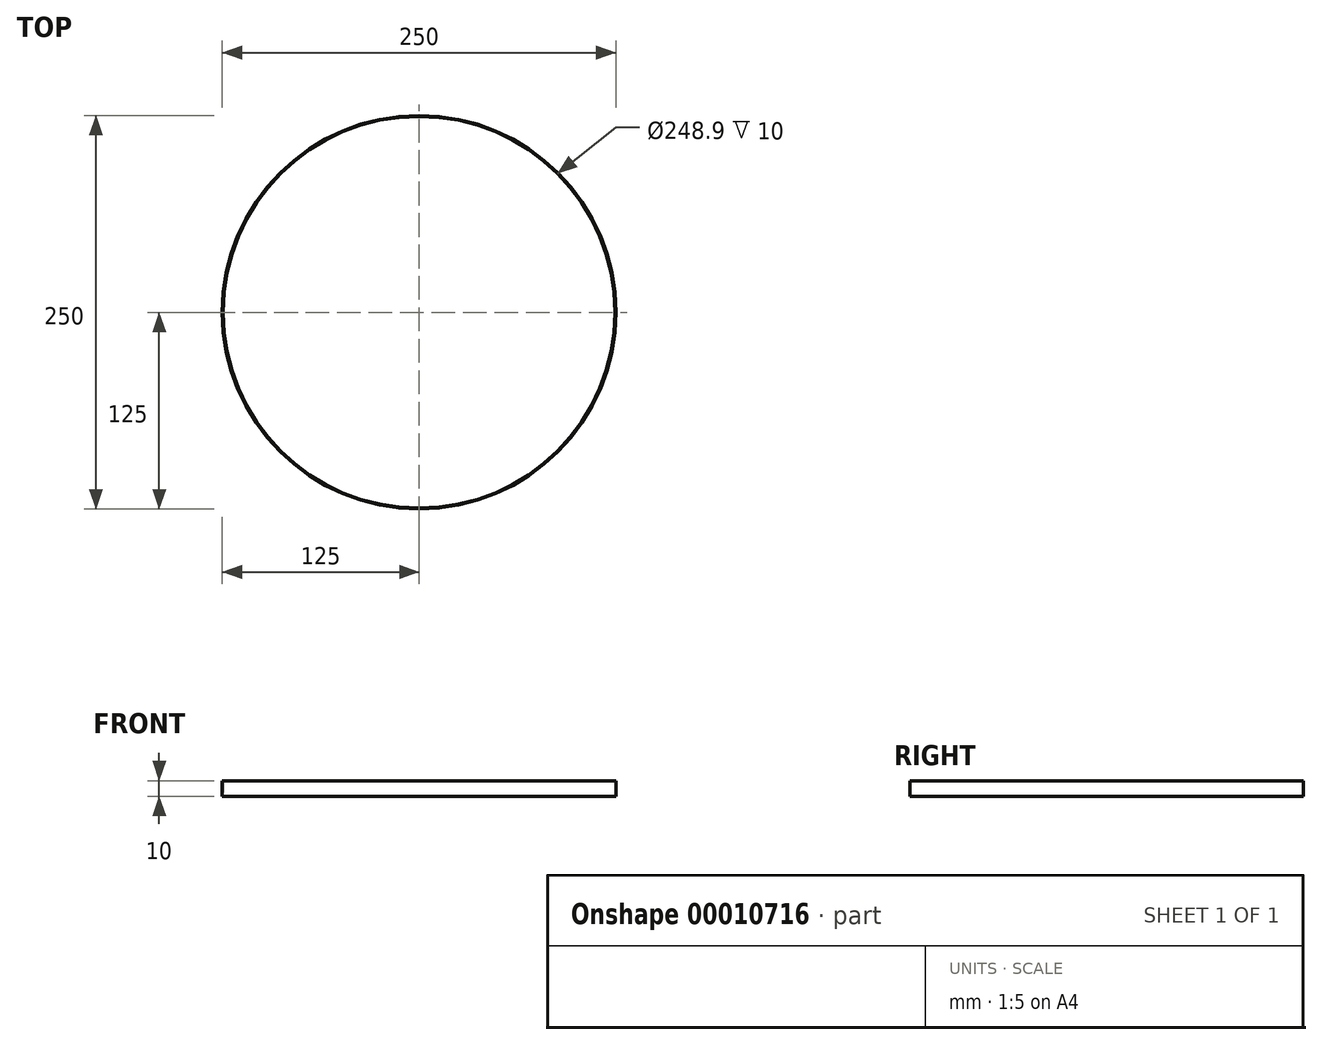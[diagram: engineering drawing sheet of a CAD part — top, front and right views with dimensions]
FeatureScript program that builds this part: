
annotation { "Feature Type Name" : "Feature", "Feature Type Description" : "" }
export const myFeature = defineFeature(function(context is Context, id is Id, definition is map)
    precondition{}
    {
        {
            var Q0;
            Q0=qCreatedBy(makeId("Top.planeOp"),FACE);
            var sketch = newSketch(context, id + "F0", { "sketchPlane" : qUnion([Q0])});
            skCircle(sketch, "E0", {"center": v(0, 0) * mm, "radius": 124.45 * mm});
            skCircle(sketch, "E1", {"center": v(0, 0) * mm, "radius": 125 * mm});
            skSolve(sketch);
        }
        {
            var Q0;
            Q0=makeQuery(id+"F0.imprint","IMPRINT",FACE,{"disambiguationData":[TD([[makeQuery(id+"F0.imprint","IMPRINT",EDGE,{"derivedFrom":sQuery(id+"F0.wireOp",EDGE,"E0")}),-1.0]])]});
            extrude(context, id + "F1", {"entities" : qUnion([Q0]), "depth" : 10 * mm});
        }
    });
